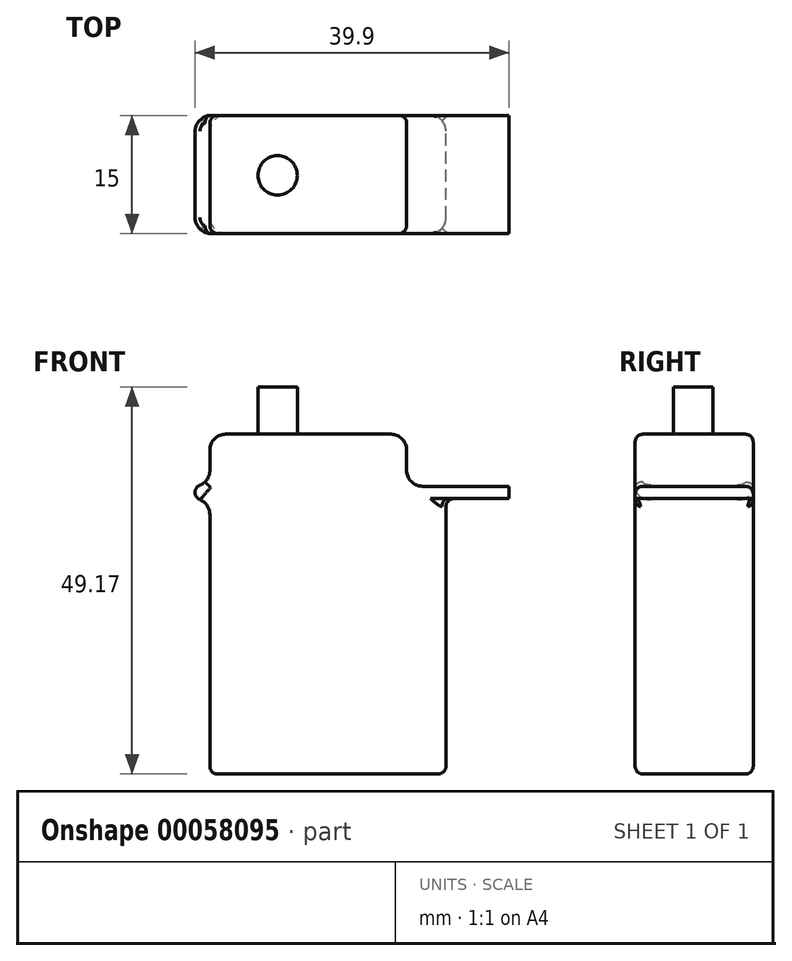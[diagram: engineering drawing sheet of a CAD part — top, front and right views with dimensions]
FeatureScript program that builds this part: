
annotation { "Feature Type Name" : "Feature", "Feature Type Description" : "" }
export const myFeature = defineFeature(function(context is Context, id is Id, definition is map)
    precondition{}
    {
        {
            var Q0;
            Q0=qCreatedBy(makeId("Front.planeOp"),FACE);
            var sketch = newSketch(context, id + "F0", { "sketchPlane" : qUnion([Q0])});
            skLineSegment(sketch, "E0.top", {"start": v(5, -6.46) * mm, "end": v(-25, -6.46) * mm});
            skLineSegment(sketch, "E0.left", {"start": v(5, 28.54) * mm, "end": v(5, -6.46) * mm});
            skLineSegment(sketch, "E0.right", {"start": v(-25, 26.54) * mm, "end": v(-25, -6.46) * mm});
            skLineSegment(sketch, "E1.bottom", {"start": v(-30, 28.54) * mm, "end": v(-27, 28.54) * mm});
            skLineSegment(sketch, "E1.top", {"start": v(2, 30.1) * mm, "end": v(13.02, 30.1) * mm});
            skLineSegment(sketch, "E1.left", {"start": v(-30, 28.54) * mm, "end": v(-30, 30.1) * mm});
            skLineSegment(sketch, "E1.right", {"start": v(13.02, 28.54) * mm, "end": v(13.02, 30.1) * mm});
            skLineSegment(sketch, "E2.trimOffspring", {"start": v(5, 28.54) * mm, "end": v(13.02, 28.54) * mm});
            skLineSegment(sketch, "E3.top", {"start": v(-23, 36.71) * mm, "end": v(-2, 36.71) * mm});
            skLineSegment(sketch, "E3.left", {"start": v(-25, 32.1) * mm, "end": v(-25, 34.71) * mm});
            skLineSegment(sketch, "E3.right", {"start": v(0, 32.1) * mm, "end": v(0, 34.71) * mm});
            skArc(sketch, "E4.filletArc", {"start": v(0, 32.1) * mm, "mid": v(0.59, 30.69) * mm, "end": v(2, 30.1) * mm});
            skLineSegment(sketch, "E5", {"start": v(-30, 30.1) * mm, "end": v(-27, 30.1) * mm});
            skLineSegment(sketch, "E6", {"start": v(-25, 30.1) * mm, "end": v(-25, 30.1) * mm});
            skLineSegment(sketch, "E7", {"start": v(-25, 32.1) * mm, "end": v(-25, 32.1) * mm});
            skPoint(sketch, "E8.visualSharp", {"position": v(-25, 36.71) * mm});
            skArc(sketch, "E8.filletArc", {"start": v(-23, 36.71) * mm, "mid": v(-24.41, 36.13) * mm, "end": v(-25, 34.71) * mm});
            skPoint(sketch, "E9.visualSharp", {"position": v(0, 36.71) * mm});
            skArc(sketch, "E9.filletArc", {"start": v(0, 34.71) * mm, "mid": v(-0.59, 36.13) * mm, "end": v(-2, 36.71) * mm});
            skPoint(sketch, "E10.visualSharp", {"position": v(-25, 28.54) * mm});
            skArc(sketch, "E10.filletArc", {"start": v(-25, 26.54) * mm, "mid": v(-25.59, 27.95) * mm, "end": v(-27, 28.54) * mm});
            skPoint(sketch, "E11.visualSharp", {"position": v(-25, 30.1) * mm});
            skArc(sketch, "E11.filletArc", {"start": v(-27, 30.1) * mm, "mid": v(-25.59, 30.69) * mm, "end": v(-25, 32.1) * mm});
            skSolve(sketch);
        }
        {
            var Q0;
            Q0=makeQuery(id+"F0.imprint","IMPRINT",FACE,{"disambiguationData":[TD([[makeQuery(id+"F0.imprint","IMPRINT",EDGE,{"derivedFrom":sQuery(id+"F0.wireOp",EDGE,"E0.top")}),-1.0]])]});
            extrude(context, id + "F1", {"entities" : qUnion([Q0]), "depth" : 15 * mm});
        }
        {
            var Q0;
            Q0=makeQuery(id+"F1.opExtrude","CAP_EDGE",EDGE,{"disambiguationData":[OSD([sQuery(id+"F0.wireOp",EDGE,"E0.right")])],"isStart":false});
            var Q1;
            Q1=makeQuery(id+"F1.opExtrude","CAP_EDGE",EDGE,{"disambiguationData":[OSD([sQuery(id+"F0.wireOp",EDGE,"E0.left")])],"isStart":false});
            var Q2;
            Q2=makeQuery(id+"F1.opExtrude","CAP_EDGE",EDGE,{"disambiguationData":[OSD([sQuery(id+"F0.wireOp",EDGE,"E0.left")])],"isStart":true});
            var Q3;
            Q3=makeQuery(id+"F1.opExtrude","CAP_EDGE",EDGE,{"disambiguationData":[OSD([sQuery(id+"F0.wireOp",EDGE,"E0.right")])],"isStart":true});
            fillet(context, id + "F2", {"entities" : qUnion([Q0, Q1, Q2, Q3]), "radius" : 2 * mm, "tangentPropagation" : true, "allowEdgeOverflow" : false});
        }
        {
            var Q0;
            Q0=makeQuery(id+"F1.opExtrude","CAP_EDGE",EDGE,{"disambiguationData":[OSD([sQuery(id+"F0.wireOp",EDGE,"E0.top")])],"isStart":false});
            var Q1;
            Q1=makeQuery(id+"F1.opExtrude","SWEPT_EDGE",EDGE,{"disambiguationData":[OSD([sQuery(id+"F0.wireOp",EDGE,"E0.left"),sQuery(id+"F0.wireOp",EDGE,"E2.trimOffspring")])]});
            var Q2;
            Q2=makeQuery(id+"F1.opExtrude","CAP_EDGE",EDGE,{"disambiguationData":[OSD([sQuery(id+"F0.wireOp",EDGE,"E8.filletArc")])],"isStart":false});
            fillet(context, id + "F3", {"entities" : qUnion([Q0, Q1, Q2]), "radius" : 1 * mm, "tangentPropagation" : true, "allowEdgeOverflow" : false});
        }
        {
            var Q0;
            Q0=makeQuery(id+"F1.opExtrude","SWEPT_FACE",FACE,{"disambiguationData":[OSD([sQuery(id+"F0.wireOp",EDGE,"E3.top")])]});
            var sketch = newSketch(context, id + "F4", { "sketchPlane" : qUnion([Q0])});
            skCircle(sketch, "E12", {"center": v(-16.39, -7.61) * mm, "radius": 2.5 * mm});
            skSolve(sketch);
        }
        {
            var Q0;
            Q0 = qSketchRegion(id + "F4", true);
            var Q1;
            Q1=makeQuery(id+"F4.imprint","IMPRINT",FACE,{"disambiguationData":[TD([[makeQuery(id+"F4.imprint","IMPRINT",EDGE,{"derivedFrom":sQuery(id+"F4.wireOp",EDGE,"E12")}),1.0]])]});
            extrude(context, id + "F5", {"entities" : qUnion([Q0, Q1]), "operationType" : NewBodyOperationType.ADD, "depth" : 6 * mm});
        }
    });
